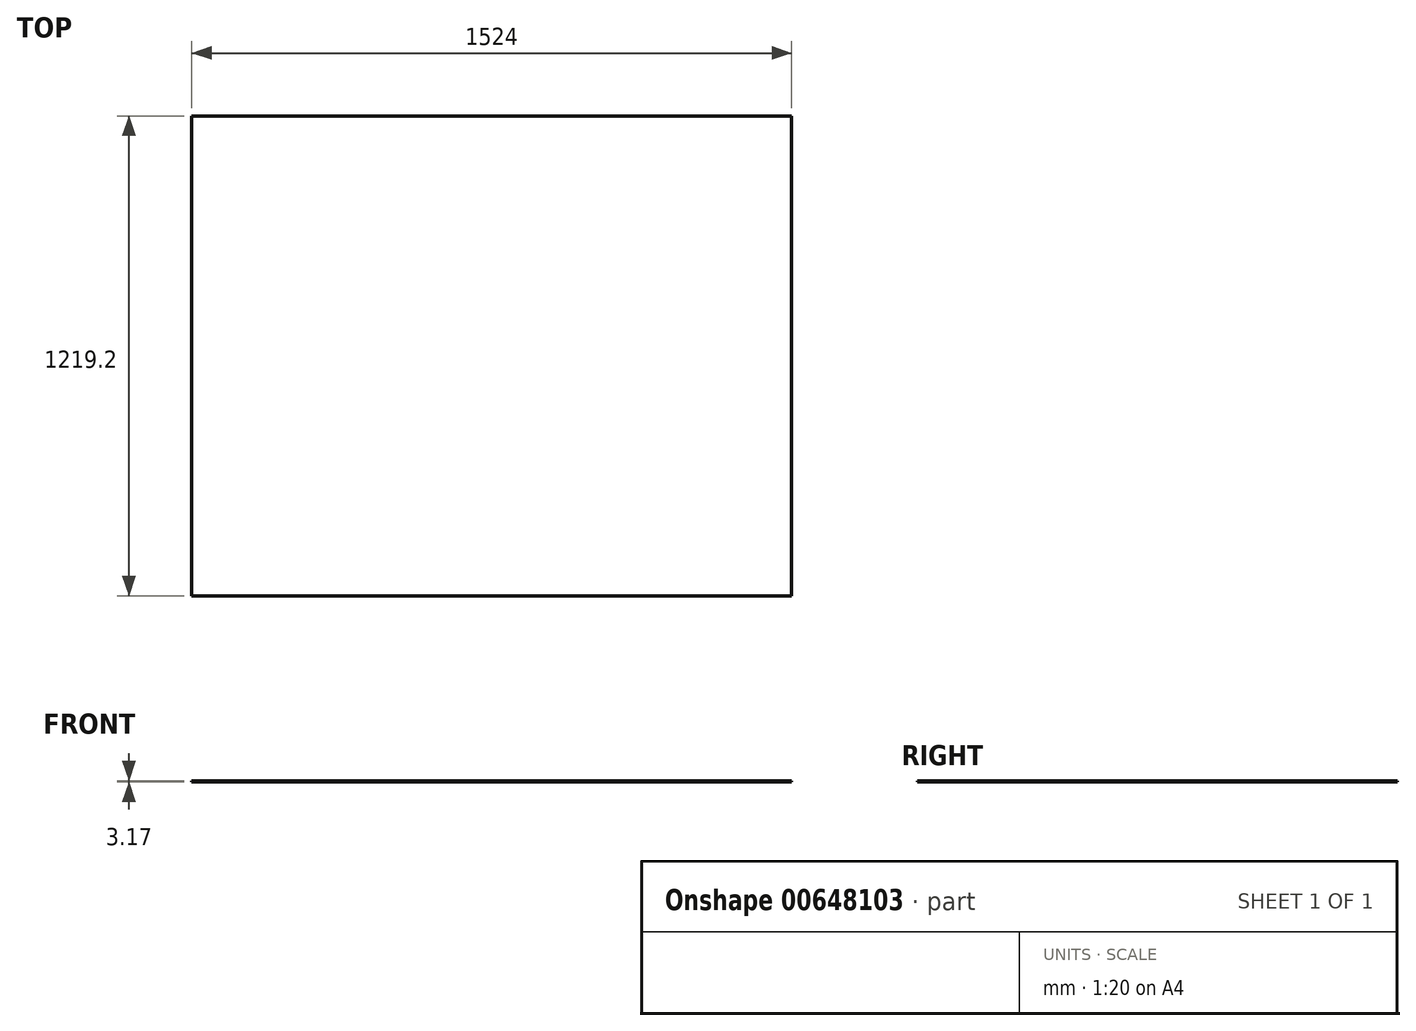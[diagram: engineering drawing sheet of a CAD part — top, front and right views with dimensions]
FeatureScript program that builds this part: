
annotation { "Feature Type Name" : "Feature", "Feature Type Description" : "" }
export const myFeature = defineFeature(function(context is Context, id is Id, definition is map)
    precondition{}
    {
        {
            var Q0;
            Q0=qCreatedBy(makeId("Top.planeOp"),FACE);
            var sketch = newSketch(context, id + "F0", { "sketchPlane" : qUnion([Q0])});
            skLineSegment(sketch, "E0.bottom", {"start": v(762, -609.6) * mm, "end": v(-762, -609.6) * mm});
            skLineSegment(sketch, "E0.top", {"start": v(762, 609.6) * mm, "end": v(-762, 609.6) * mm});
            skLineSegment(sketch, "E0.left", {"start": v(762, -609.6) * mm, "end": v(762, 609.6) * mm});
            skLineSegment(sketch, "E0.right", {"start": v(-762, -609.6) * mm, "end": v(-762, 609.6) * mm});
            skPoint(sketch, "E0.middle", {"position": v(0, 0) * mm});
            skSolve(sketch);
        }
        {
            var Q0;
            Q0 = qSketchRegion(id + "F0", true);
            extrude(context, id + "F1", {"entities" : qUnion([Q0]), "depth" : 3.17 * mm, "offsetDistance" : 25.4 * mm});
        }
    });
